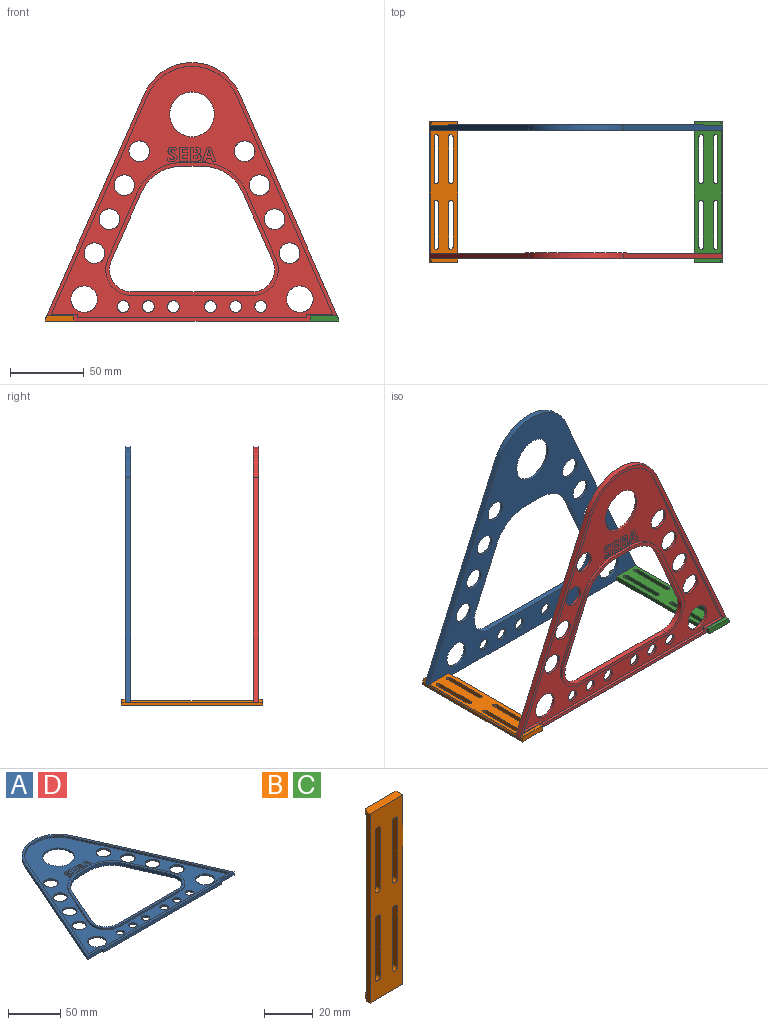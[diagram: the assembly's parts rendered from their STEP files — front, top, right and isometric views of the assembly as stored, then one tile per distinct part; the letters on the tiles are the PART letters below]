
ASSEMBLY  parts=4 mates=2
PART A: 137 faces, bbox 198.1x175x3.8 mm
  f0: plane 190.48x170mm, normal (0,0,1), area 8661.7mm2, adj f15,f16,f17,f18,f19,f20,f21,f22
  f1: plane 19.07x3.75mm, normal (0,-1,0), area 71.5mm2, adj f2,f33,f34,f43
  f2: plane 152.02x67.05mm, normal (0.91,0.4,0), area 623.1mm2, adj f1,f3,f34,f43
  f3: cylinder r=35mm len=64.05mm, axis (0,0,-1), area 303.3mm2, adj f2,f4,f34,f43
  f4: plane 152.02x67.05mm, normal (-0.91,0.4,0), area 623.1mm2, adj f3,f5,f34,f43
  f5: plane 19.07x3.75mm, normal (0,-1,0), area 71.5mm2, adj f4,f6,f34,f43
  f6: plane 3.75x2.1mm, normal (-1,0,0), area 7.9mm2, adj f5,f7,f34,f43
  f7: plane 160x3.75mm, normal (0,-1,0), area 600mm2, adj f6,f33,f34,f43
  f8: cylinder r=30mm len=27.45mm, axis (0,0,-1), area 130mm2, adj f9,f32,f34,f52
  f9: plane 13.71x3.75mm, normal (0,-1,0), area 51.4mm2, adj f8,f10,f34,f52
  f10: cylinder r=30mm len=27.45mm, axis (0,0,-1), area 130mm2, adj f9,f11,f34,f52
  f11: plane 45.95x20.27mm, normal (-0.91,-0.4,0), area 188.3mm2, adj f10,f12,f34,f52
  f12: cylinder r=15mm len=21.05mm, axis (0,0,-1), area 111.7mm2, adj f11,f13,f34,f52
  f13: plane 81.69x3.75mm, normal (0,1,0), area 306.3mm2, adj f12,f14,f34,f52
  f14: cylinder r=15mm len=21.05mm, axis (0,0,-1), area 111.7mm2, adj f13,f32,f34,f52
  f15: cylinder r=15.1mm len=30.2mm, axis (0,0,-1), area 166mm2, adj f0,f34
  f16: cylinder r=9mm len=18mm, axis (0,0,-1), area 99mm2, adj f0,f34
  f17: cylinder r=7mm len=14mm, axis (0,0,-1), area 77mm2, adj f0,f34
  f18: cylinder r=7mm len=14mm, axis (0,0,-1), area 77mm2, adj f0,f34
  f19: cylinder r=7mm len=14mm, axis (0,0,-1), area 77mm2, adj f0,f34
  f20: cylinder r=9mm len=18mm, axis (0,0,-1), area 99mm2, adj f0,f34
  f21: cylinder r=7mm len=14mm, axis (0,0,-1), area 77mm2, adj f0,f34
  f22: cylinder r=4mm len=8mm, axis (0,0,-1), area 44mm2, adj f0,f34
  f23: cylinder r=4mm len=8mm, axis (0,0,-1), area 44mm2, adj f0,f34
  f24: cylinder r=4mm len=8mm, axis (0,0,-1), area 44mm2, adj f0,f34
  f25: cylinder r=4mm len=8mm, axis (0,0,-1), area 44mm2, adj f0,f34
  f26: cylinder r=4mm len=8mm, axis (0,0,-1), area 44mm2, adj f0,f34
  f27: cylinder r=4mm len=8mm, axis (0,0,-1), area 44mm2, adj f0,f34
  f28: cylinder r=7mm len=14mm, axis (0,0,-1), area 77mm2, adj f0,f34
  f29: cylinder r=7mm len=14mm, axis (0,0,-1), area 77mm2, adj f0,f34
  f30: cylinder r=7mm len=14mm, axis (0,0,-1), area 77mm2, adj f0,f34
  f31: cylinder r=7mm len=14mm, axis (0,0,-1), area 77mm2, adj f0,f34
  f32: plane 45.95x20.27mm, normal (0.91,-0.4,0), area 188.3mm2, adj f8,f14,f34,f52
  f33: plane 3.75x2.1mm, normal (1,0,0), area 7.9mm2, adj f1,f7,f34,f43
  f34: plane 198.15x175mm, normal (0,0,-1), area 11184.1mm2, adj f1,f2,f3,f4,f5,f6,f7,f8
  f35: plane 17.74x2mm, normal (0,1,0), area 35.5mm2, adj f0,f36,f42,f43
  f36: plane 148.52x65.5mm, normal (0.91,-0.4,0), area 324.6mm2, adj f0,f35,f37,f43
  f37: cylinder r=32.5mm len=59.47mm, axis (0,0,-1), area 150.2mm2, adj f0,f36,f38,f43
  f38: plane 148.52x65.5mm, normal (-0.91,-0.4,0), area 324.6mm2, adj f0,f37,f39,f43
  f39: plane 17.74x2mm, normal (0,1,0), area 35.5mm2, adj f0,f38,f40,f43
  f40: plane 2.1x2mm, normal (-1,0,0), area 4.2mm2, adj f0,f39,f41,f43
  f41: plane 155x2mm, normal (0,1,0), area 310mm2, adj f0,f40,f42,f43
  f42: plane 2.1x2mm, normal (1,0,0), area 4.2mm2, adj f0,f35,f41,f43
  f43: plane 198.15x175mm, normal (0,0,1), area 1512.4mm2, adj f1,f2,f3,f4,f5,f6,f7,f33
  f44: plane 13.71x2mm, normal (0,1,0), area 27.4mm2, adj f0,f45,f51,f52
  f45: cylinder r=32.5mm len=29.74mm, axis (0,0,-1), area 75.1mm2, adj f0,f44,f46,f52
  f46: plane 45.95x20.27mm, normal (-0.91,0.4,0), area 100.4mm2, adj f0,f45,f47,f52
  f47: cylinder r=17.5mm len=24.56mm, axis (0,0,-1), area 69.5mm2, adj f0,f46,f48,f52
  f48: plane 81.69x2mm, normal (0,-1,0), area 163.4mm2, adj f0,f47,f49,f52
  f49: cylinder r=17.5mm len=24.56mm, axis (0,0,-1), area 69.5mm2, adj f0,f48,f50,f52
  f50: plane 45.95x20.27mm, normal (0.91,0.4,0), area 100.4mm2, adj f0,f49,f51,f52
  f51: cylinder r=32.5mm len=29.74mm, axis (0,0,-1), area 75.1mm2, adj f0,f44,f50,f52
  f52: plane 116.69x89.9mm, normal (0,0,1), area 831.5mm2, adj f8,f9,f10,f11,f12,f13,f14,f32
  f53: extruded ~2.04x0.93mm, area 0.6mm2, adj f0,f54,f80,f81
  f54: extruded ~1.57x0.5mm, area 0.4mm2, adj f0,f53,f55,f81
  f55: extruded ~1.83x1.28mm, area 0.6mm2, adj f0,f54,f56,f81
  f56: extruded ~1.28x0.67mm, area 0.4mm2, adj f0,f55,f57,f81
  f57: extruded ~0.39x0.39mm, area 0.1mm2, adj f0,f56,f58,f81
  f58: extruded ~0.47x0.25mm, area 0.1mm2, adj f0,f57,f59,f81
  f59: extruded ~0.7x0.31mm, area 0.2mm2, adj f0,f58,f60,f81
  f60: extruded ~0.88x0.27mm, area 0.2mm2, adj f0,f59,f61,f81
  f61: extruded ~0.98x0.25mm, area 0.2mm2, adj f0,f60,f62,f81
  f62: extruded ~1.26x0.44mm, area 0.3mm2, adj f0,f61,f63,f81
  f63: plane 1.57x0.65mm, normal (0.92,-0.38,0), area 0.4mm2, adj f0,f62,f64,f81
  f64: extruded ~1.41x0.49mm, area 0.4mm2, adj f0,f63,f65,f81
  f65: extruded ~1.42x0.25mm, area 0.4mm2, adj f0,f64,f66,f81
  f66: extruded ~2.37x0.72mm, area 0.6mm2, adj f0,f65,f67,f81
  f67: extruded ~1.99x0.86mm, area 0.6mm2, adj f0,f66,f68,f81
  f68: extruded ~1.17x0.26mm, area 0.3mm2, adj f0,f67,f69,f81
  f69: extruded ~0.88x0.7mm, area 0.3mm2, adj f0,f68,f70,f81
  f70: extruded ~1.31x0.79mm, area 0.4mm2, adj f0,f69,f71,f81
  f71: extruded ~1.24x0.65mm, area 0.3mm2, adj f0,f70,f72,f81
  f72: extruded ~0.46x0.42mm, area 0.2mm2, adj f0,f71,f73,f81
  f73: extruded ~0.5x0.25mm, area 0.1mm2, adj f0,f72,f74,f81
  f74: extruded ~0.76x0.36mm, area 0.2mm2, adj f0,f73,f75,f81
  f75: extruded ~1.02x0.25mm, area 0.3mm2, adj f0,f74,f76,f81
  f76: extruded ~1.22x0.25mm, area 0.3mm2, adj f0,f75,f77,f81
  f77: extruded ~1.63x0.61mm, area 0.4mm2, adj f0,f76,f78,f81
  f78: plane 1.88x0.25mm, normal (-1,0,0), area 0.5mm2, adj f0,f77,f79,f81
  f79: extruded ~2.7x0.58mm, area 0.7mm2, adj f0,f78,f80,f81
  f80: extruded ~2.58x0.74mm, area 0.7mm2, adj f0,f53,f79,f81
  f81: plane 9.8x6.22mm, normal (0,0,1), area 34.3mm2, adj f53,f54,f55,f56,f57,f58,f59,f60
  f82: plane 5.49x0.25mm, normal (0,-1,0), area 1.4mm2, adj f0,f83,f93,f94
  f83: plane 1.67x0.25mm, normal (1,0,0), area 0.4mm2, adj f0,f82,f84,f94
  f84: plane 3.47x0.25mm, normal (0,1,0), area 0.9mm2, adj f0,f83,f85,f94
  f85: plane 2.46x0.25mm, normal (1,0,0), area 0.6mm2, adj f0,f84,f86,f94
  f86: plane 3.23x0.25mm, normal (0,-1,0), area 0.8mm2, adj f0,f85,f87,f94
  f87: plane 1.66x0.25mm, normal (1,0,0), area 0.4mm2, adj f0,f86,f88,f94
  f88: plane 3.23x0.25mm, normal (0,1,0), area 0.8mm2, adj f0,f87,f89,f94
  f89: plane 2.09x0.25mm, normal (1,0,0), area 0.5mm2, adj f0,f88,f90,f94
  f90: plane 3.47x0.25mm, normal (0,-1,0), area 0.9mm2, adj f0,f89,f91,f94
  f91: plane 1.66x0.25mm, normal (1,0,0), area 0.4mm2, adj f0,f90,f92,f94
  f92: plane 5.49x0.25mm, normal (0,1,0), area 1.4mm2, adj f0,f91,f93,f94
  f93: plane 9.54x0.25mm, normal (-1,0,0), area 2.4mm2, adj f0,f82,f92,f94
  f94: plane 9.54x5.49mm, normal (0,0,1), area 36.2mm2, adj f82,f83,f84,f85,f86,f87,f88,f89
  f95: plane 2.49x0.25mm, normal (1,0,0), area 0.6mm2, adj f96,f119,f120,f121
  f96: plane 1.25x0.25mm, normal (0,-1,0), area 0.3mm2, adj f95,f97,f120,f121
  f97: extruded ~1.69x1.19mm, area 0.6mm2, adj f96,f98,f120,f121
  f98: extruded ~0.98x0.4mm, area 0.3mm2, adj f97,f99,f120,f121
  f99: extruded ~1.23x0.32mm, area 0.3mm2, adj f98,f119,f120,f121
  f100: plane 1.17x0.25mm, normal (0,1,0), area 0.3mm2, adj f101,f117,f120,f122
  f101: plane 2.12x0.25mm, normal (1,0,0), area 0.5mm2, adj f100,f102,f120,f122
  f102: plane 1.06x0.25mm, normal (0,-1,0), area 0.3mm2, adj f101,f103,f120,f122
  f103: extruded ~1.27x0.25mm, area 0.3mm2, adj f102,f104,f120,f122
  f104: extruded ~0.79x0.4mm, area 0.2mm2, adj f103,f105,f120,f122
  f105: extruded ~0.84x0.37mm, area 0.2mm2, adj f104,f117,f120,f122
  f106: plane 2.97x0.25mm, normal (0,1,0), area 0.7mm2, adj f0,f107,f118,f120
  f107: plane 9.54x0.25mm, normal (-1,0,0), area 2.4mm2, adj f0,f106,f108,f120
  f108: plane 3.57x0.25mm, normal (0,-1,0), area 0.9mm2, adj f0,f107,f109,f120
  f109: extruded ~2.56x0.73mm, area 0.7mm2, adj f0,f108,f110,f120
  f110: extruded ~2.03x0.94mm, area 0.6mm2, adj f0,f109,f111,f120
  f111: extruded ~1.47x0.4mm, area 0.4mm2, adj f0,f110,f112,f120
  f112: extruded ~1.31x0.76mm, area 0.4mm2, adj f0,f111,f113,f120
  f113: plane 0.25x0.06mm, normal (1,0,0), area 0mm2, adj f0,f112,f114,f120
  f114: extruded ~1.07x0.66mm, area 0.3mm2, adj f0,f113,f115,f120
  f115: extruded ~1.4x0.4mm, area 0.4mm2, adj f0,f114,f116,f120
  f116: extruded ~1.84x0.92mm, area 0.5mm2, adj f0,f115,f118,f120
  f117: extruded ~1.19x0.25mm, area 0.3mm2, adj f100,f105,f120,f122
  f118: extruded ~2.94x0.58mm, area 0.8mm2, adj f0,f106,f116,f120
  f119: plane 1.32x0.25mm, normal (0,1,0), area 0.3mm2, adj f95,f99,f120,f121
  f120: plane 9.54x7.07mm, normal (0,0,1), area 49.6mm2, adj f95,f96,f97,f98,f99,f100,f101,f102
  f121: plane 2.95x2.49mm, normal (0,0,1), area 6.6mm2, adj f95,f96,f97,f98,f99,f119
  f122: plane 2.73x2.12mm, normal (0,0,1), area 5.3mm2, adj f100,f101,f102,f103,f104,f105,f117
  f123: extruded ~3.49x1.08mm, area 0.9mm2, adj f124,f134,f135,f136
  f124: plane 2.48x0.25mm, normal (0,1,0), area 0.6mm2, adj f123,f125,f135,f136
  f125: extruded ~4.13x1.23mm, area 1.1mm2, adj f124,f134,f135,f136
  f126: plane 2.27x0.69mm, normal (-0.96,-0.29,0), area 0.6mm2, adj f0,f127,f133,f135
  f127: plane 2.18x0.25mm, normal (0,-1,0), area 0.5mm2, adj f0,f126,f128,f135
  f128: plane 9.58x3.38mm, normal (0.94,0.33,0), area 2.5mm2, adj f0,f127,f129,f135
  f129: plane 2.47x0.25mm, normal (0,1,0), area 0.6mm2, adj f0,f128,f130,f135
  f130: plane 9.58x3.37mm, normal (-0.94,0.33,0), area 2.5mm2, adj f0,f129,f131,f135
  f131: plane 2.18x0.25mm, normal (0,-1,0), area 0.5mm2, adj f0,f130,f132,f135
  f132: plane 2.27x0.69mm, normal (0.96,-0.29,0), area 0.6mm2, adj f0,f131,f133,f135
  f133: plane 3.48x0.25mm, normal (0,-1,0), area 0.9mm2, adj f0,f126,f132,f135
  f134: extruded ~0.64x0.25mm, area 0.2mm2, adj f123,f125,f135,f136
  f135: plane 9.58x9.22mm, normal (0,0,1), area 41.5mm2, adj f123,f124,f125,f126,f127,f128,f129,f130
  f136: plane 4.13x2.48mm, normal (0,0,1), area 5mm2, adj f123,f124,f125,f134
PART B: 33 faces, bbox 19.1x4x95.4 mm
  f0: plane 95.43x19.07mm, normal (0,-1,0), area 1431.8mm2, adj f3,f4,f9,f10,f11,f12,f13,f14
  f1: plane 83x18.47mm, normal (0,1,0), area 1145.1mm2, adj f4,f6,f7,f8,f9,f10,f11,f12
  f2: plane 19.05x3.75mm, normal (0,1,0), area 71.4mm2, adj f4,f6,f8,f28
  f3: plane 95.43x1.9mm, normal (-1,0,0), area 177.8mm2, adj f0,f8,f25,f26,f28,f29,f31,f32
  f4: plane 95.43x4mm, normal (1,0,0), area 274.6mm2, adj f0,f1,f2,f5,f6,f7,f25,f26
  f5: plane 19.05x3.75mm, normal (0,1,0), area 71.4mm2, adj f4,f7,f8,f25
  f6: plane 19.05x1mm, normal (0,0,1), area 18.8mm2, adj f1,f2,f4,f8
  f7: plane 19.05x1mm, normal (0,0,-1), area 18.8mm2, adj f1,f4,f5,f8
  f8: plane 90.5x1.04mm, normal (-0.87,0.5,0), area 99.9mm2, adj f1,f2,f3,f5,f6,f7,f25,f28
  f9: plane 30x2.9mm, normal (-1,0,0), area 87mm2, adj f0,f1,f10,f12
  f10: cylinder r=1.5mm len=3mm, axis (0,-1,0), area 13.7mm2, adj f0,f1,f9,f11
  f11: plane 30x2.9mm, normal (1,0,0), area 87mm2, adj f0,f1,f10,f12
  f12: cylinder r=1.5mm len=3mm, axis (0,-1,0), area 13.7mm2, adj f0,f1,f9,f11
  f13: plane 30x2.9mm, normal (1,0,0), area 87mm2, adj f0,f1,f14,f16
  f14: cylinder r=1.5mm len=3mm, axis (0,-1,0), area 13.7mm2, adj f0,f1,f13,f15
  f15: plane 30x2.9mm, normal (-1,0,0), area 87mm2, adj f0,f1,f14,f16
  f16: cylinder r=1.5mm len=3mm, axis (0,-1,0), area 13.7mm2, adj f0,f1,f13,f15
  f17: cylinder r=1.5mm len=3mm, axis (0,-1,0), area 13.7mm2, adj f0,f1,f18,f20
  f18: plane 30x2.9mm, normal (-1,0,0), area 87mm2, adj f0,f1,f17,f19
  f19: cylinder r=1.5mm len=3mm, axis (0,-1,0), area 13.7mm2, adj f0,f1,f18,f20
  f20: plane 30x2.9mm, normal (1,0,0), area 87mm2, adj f0,f1,f17,f19
  f21: cylinder r=1.5mm len=3mm, axis (0,-1,0), area 13.7mm2, adj f0,f1,f22,f24
  f22: plane 30x2.9mm, normal (-1,0,0), area 87mm2, adj f0,f1,f21,f23
  f23: cylinder r=1.5mm len=3mm, axis (0,-1,0), area 13.7mm2, adj f0,f1,f22,f24
  f24: plane 30x2.9mm, normal (1,0,0), area 87mm2, adj f0,f1,f21,f23
  f25: plane 19.07x2.14mm, normal (0,0,1), area 38.8mm2, adj f3,f4,f5,f8,f27,f32
  f26: plane 19.07x4mm, normal (0,0,-1), area 75mm2, adj f0,f3,f4,f27,f32
  f27: plane 17.86x2.46mm, normal (0,1,0), area 44mm2, adj f4,f25,f26,f32
  f28: plane 19.07x2.14mm, normal (0,0,-1), area 38.8mm2, adj f2,f3,f4,f8,f30,f31
  f29: plane 19.07x4mm, normal (0,0,1), area 75mm2, adj f0,f3,f4,f30,f31
  f30: plane 17.86x2.46mm, normal (0,1,0), area 44mm2, adj f4,f28,f29,f31
  f31: plane 2.46x2.1mm, normal (-0.87,0.5,0), area 6mm2, adj f3,f28,f29,f30
  f32: plane 2.46x2.1mm, normal (-0.87,0.5,0), area 6mm2, adj f3,f25,f26,f27
PART C: same geometry as B
PART D: same geometry as A
PLACE A rot(axis=(0,0.71,0.71),180deg) t=(0,83,-140)mm
PLACE B rot(axis=(1,0,0),90deg) t=(-99.07,-3.75,-137.9)mm
PLACE C rot(axis=(0,0.71,0.71),180deg) t=(99.09,86.75,-137.9)mm
PLACE D rot(axis=(1,0,0),90deg) t=(0,0,-140)mm fixed
MATE planar C.f5 <-> D.f1  axis (0,0,1) through (89.54,-1.88,-137.9)mm
MATE planar A.f3 <-> D.f15  axis (0,-1,0) through (0,83,0)mm
